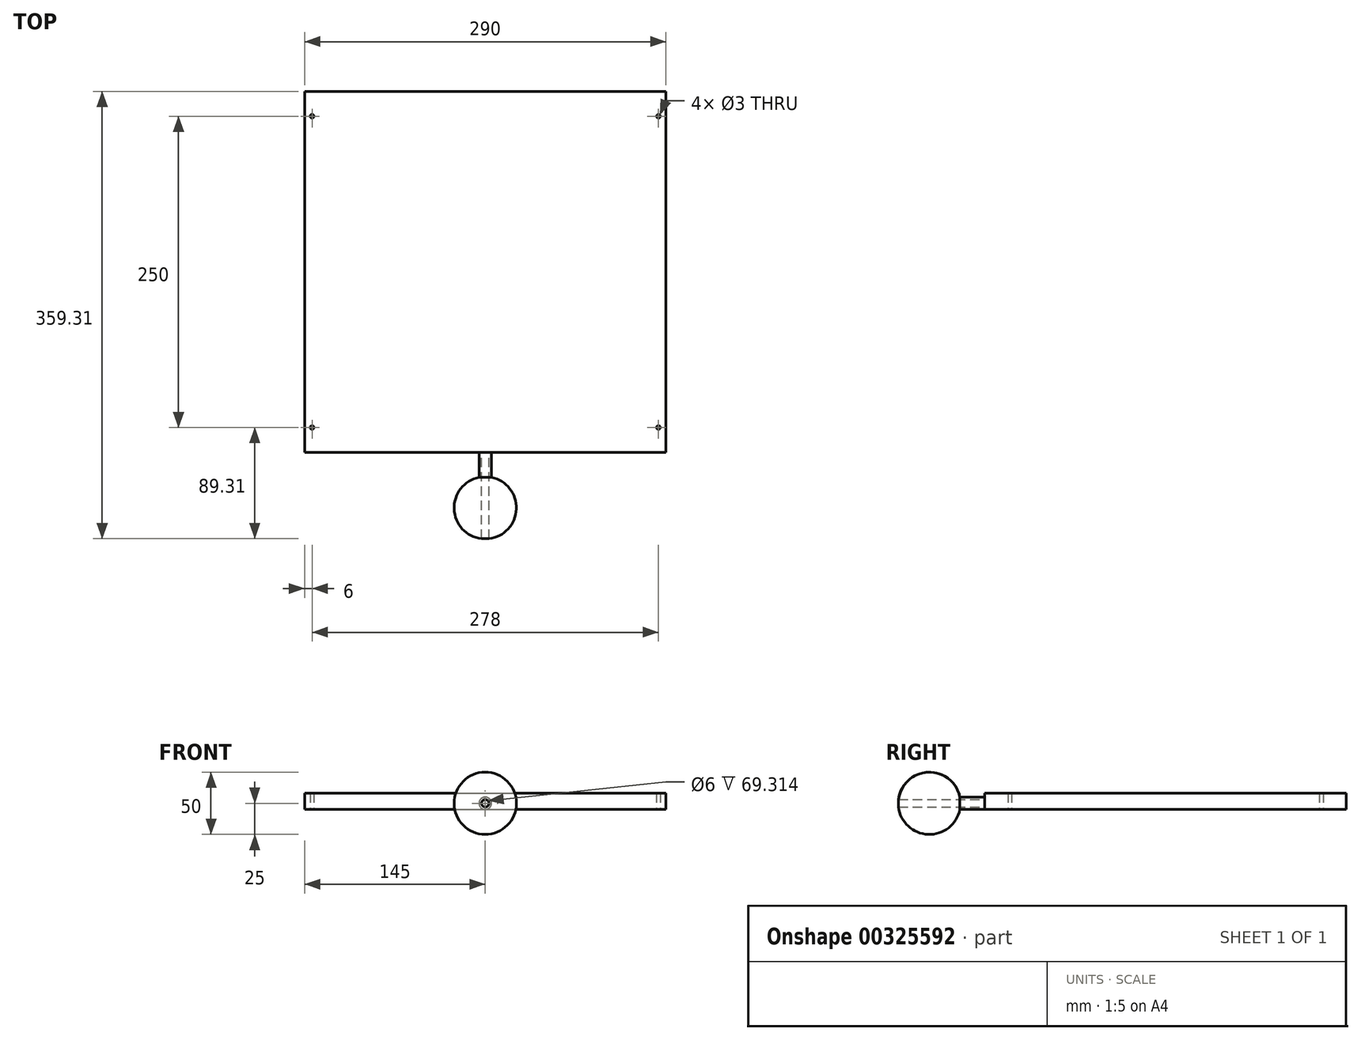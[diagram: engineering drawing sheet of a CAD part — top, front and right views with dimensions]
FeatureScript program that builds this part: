
annotation { "Feature Type Name" : "Feature", "Feature Type Description" : "" }
export const myFeature = defineFeature(function(context is Context, id is Id, definition is map)
    precondition{}
    {
        {
            var Q0;
            Q0=qCreatedBy(makeId("Top.planeOp"),FACE);
            var sketch = newSketch(context, id + "F0", { "sketchPlane" : qUnion([Q0])});
            skLineSegment(sketch, "E0.bottom", {"start": v(-145, -145) * mm, "end": v(145, -145) * mm});
            skLineSegment(sketch, "E0.top", {"start": v(-145, 145) * mm, "end": v(145, 145) * mm});
            skLineSegment(sketch, "E0.left", {"start": v(-145, -145) * mm, "end": v(-145, 145) * mm});
            skLineSegment(sketch, "E0.right", {"start": v(145, -145) * mm, "end": v(145, 145) * mm});
            skPoint(sketch, "E0.middle", {"position": v(0, 0) * mm});
            skCircle(sketch, "E1", {"center": v(-139, 125) * mm, "radius": 1.5 * mm});
            skCircle(sketch, "E2", {"center": v(139, 125) * mm, "radius": 1.5 * mm});
            skCircle(sketch, "E3", {"center": v(139, -125) * mm, "radius": 1.5 * mm});
            skCircle(sketch, "E4", {"center": v(-139, -125) * mm, "radius": 1.5 * mm});
            skSolve(sketch);
        }
        {
            var Q0;
            Q0 = qSketchRegion(id + "F0", true);
            extrude(context, id + "F1", {"entities" : qUnion([Q0]), "depth" : 2 * mm});
        }
        {
            var Q0;
            Q0 = qSketchRegion(id + "F0", true);
            extrude(context, id + "F2", {"entities" : qUnion([Q0]), "oppositeDirection" : true, "depth" : 10 * mm});
        }
        {
            var Q0;
            Q0 = qSketchRegion(id + "F0", true);
            extrude(context, id + "F3", {"entities" : qUnion([Q0]), "depth" : 3 * mm});
        }
        {
            var Q0;
            Q0=makeQuery(id+"F2.opExtrude","SWEPT_EDGE",EDGE,{"disambiguationData":[OSD([sQuery(id+"F0.wireOp",EDGE,"E0.top"),sQuery(id+"F0.wireOp",EDGE,"E0.left")])]});
            cPoint(context, id + "F4", {"entities" : qUnion([Q0]), "parameter" : 0.5});
        }
        {
            var Q0;
            Q0=makeQuery(id+"F2.opExtrude","SWEPT_EDGE",EDGE,{"disambiguationData":[OSD([sQuery(id+"F0.wireOp",EDGE,"E0.bottom"),sQuery(id+"F0.wireOp",EDGE,"E0.left")])]});
            cPoint(context, id + "F5", {"entities" : qUnion([Q0]), "parameter" : 0.5});
        }
        {
            var Q0;
            Q0=makeQuery(id+"F2.opExtrude","SWEPT_EDGE",EDGE,{"disambiguationData":[OSD([sQuery(id+"F0.wireOp",EDGE,"E0.bottom"),sQuery(id+"F0.wireOp",EDGE,"E0.right")])]});
            cPoint(context, id + "F6", {"entities" : qUnion([Q0]), "parameter" : 0.5});
        }
        {
            var Q0;
            Q0 = qCreatedBy(id + "F4" ,VERTEX);
            var Q1;
            Q1 = qCreatedBy(id + "F5" ,VERTEX);
            var Q2;
            Q2 = qCreatedBy(id + "F6" ,VERTEX);
            cPlane(context, id + "F7", {"entities" : qUnion([Q0, Q1, Q2]), "cplaneType" : CPlaneType.THREE_POINT, "offset" : 25 * mm, "width" : 150 * mm, "height" : 150 * mm});
        }
        {
            var Q0;
            Q0=qCreatedBy(id+"F7.planeOp",FACE);
            var sketch = newSketch(context, id + "F8", { "sketchPlane" : qUnion([Q0])});
            skLineSegment(sketch, "E5", {"start": v(5, 145) * mm, "end": v(5, 165) * mm});
            skLineSegment(sketch, "E6", {"start": v(0, 59.45) * mm, "end": v(0, 268.13) * mm});
            skArc(sketch, "E7", {"start": v(5, 165) * mm, "mid": v(24.87, 192) * mm, "end": v(0, 214.5) * mm});
            skLineSegment(sketch, "E8", {"start": v(5, 145) * mm, "end": v(0, 145) * mm});
            skSolve(sketch);
        }
        {
            var Q0;
            Q0=makeQuery(id+"F8.imprint","IMPRINT",FACE,{"disambiguationData":[TD([[makeQuery(id+"F8.imprint","IMPRINT",EDGE,{"derivedFrom":sQuery(id+"F8.wireOp",EDGE,"E5")}),1.0]])]});
            var Q1;
            Q1=sQuery(id+"F8.wireOp",EDGE,"E6");
            revolve(context, id + "F9", {"operationType" : NewBodyOperationType.ADD, "entities" : qUnion([Q0]), "axis" : qUnion([Q1]), "revolveType" : RevolveType.FULL});
        }
        {
            var Q0;
            Q0=makeQuery(id+"F2.opExtrude","SWEPT_FACE",FACE,{"disambiguationData":[OSD([sQuery(id+"F0.wireOp",EDGE,"E0.bottom")])]});
            var sketch = newSketch(context, id + "F10", { "sketchPlane" : qUnion([Q0])});
            skCircle(sketch, "E9", {"center": v(0, -5) * mm, "radius": 3 * mm});
            skLineSegment(sketch, "E10", {"start": v(0, 0) * mm, "end": v(0, -10) * mm, "construction": true});
            skSolve(sketch);
        }
        {
            var Q0;
            Q0 = qSketchRegion(id + "F10", true);
            var Q1;
            Q1=sQuery(id+"F10.wireOp",EDGE,"lTrqH3y9-BaHe-63t5-YZRm-NKAA20vYYAJM");
            extrude(context, id + "F11", {"entities" : qUnion([Q0]), "operationType" : NewBodyOperationType.REMOVE, "surfaceEntities" : qUnion([Q1]), "depth" : 100 * mm});
        }
    });
